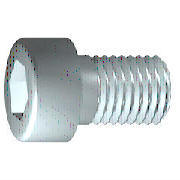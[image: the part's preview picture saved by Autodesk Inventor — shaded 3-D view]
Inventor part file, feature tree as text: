
AUTODESK INVENTOR PART (.ipt)
format: ipt  version: 2021 (Build 250183000, 183)  size: 195,072 bytes
history: native  units: mm (DEFAULTED — no unit token found)
features: sketch x2, extrude x1, plane x1, fillet x1
ambient origin geometry x7: Origin, YZ Plane, XY Plane, X Axis, Y Axis, Z Axis, Center Point
bodies: Solid1 (feature_tree), Body (feature_tree)
feature tree (5):
  extrude  "Slot"  Depth=2.5mm
  plane  "Work Plane1"
  fillet  "Fillet2"  Radius=2.5mm
  sketch  "Sketch1"  dims[d1=3.875mm d2=0.276153mm d3=2.5mm]
  sketch  "Sketch2"  dims[d4=1.1mm d5=60.0deg d6=2.5mm d7=2.5mm d8=2.309401mm d9=4.5mm d10=90.0deg d11=10.0mm d12=0.0mm d13=3.875mm d14=0.0mm d15=0.276052mm d16=0.276053mm d17=0.25mm d19=0.0mm d26=5.0mm d27=45.0deg d28=0.0mm d29=0.0mm d30=0.1mm]
